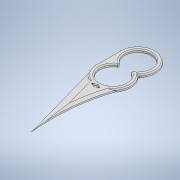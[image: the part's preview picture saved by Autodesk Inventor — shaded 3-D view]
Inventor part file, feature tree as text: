
AUTODESK INVENTOR PART (.ipt)
format: ipt  version: 2020 (Build 240168000, 168)  size: 235,008 bytes
history: native  units: in
note: dims shown in document units (in); Inventor stores cm internally (conversion verified against a paired STEP export)
features: chamfer x4, fillet x2, sketch x2, extrude x1, emboss x1
ambient origin geometry x8: Origin, YZ Plane, XZ Plane, XY Plane, X Axis, Y Axis, Z Axis, Center Point
bodies: Solid1 (feature_tree)
feature tree (10):
  extrude  "Extrusion1"  Depth=0.7in
  chamfer  "Chamfer1"  Distance=1.0in
  chamfer  "Chamfer2"  Distance=1.0in
  chamfer  "Chamfer3"  Distance=2.0in
  chamfer  "Chamfer4"  Distance=0.2in
  fillet  "Fillet5"  Radius=0.1in
  fillet  "Fillet6"  Radius=0.2in
  emboss  "Emboss1"
  sketch  "Sketch1"  dims[d0=0.75in d1=0.7in]
  sketch  "Sketch3"  dims[d2=0.75in d3=1.0in d4=1.0in d5=2.0in d6=0.2in d7=0.1in d8=0.0in d9=0.2in d10=0.05in d11=45.0deg d12=0.2in d13=0.05in d14=45.0deg d15=0.1in d16=0.03in d17=45.0deg d18=0.1in d19=0.03in d20=45.0deg d25=0.03in d26=0.03in d27=0.2in d28=0.0in]
